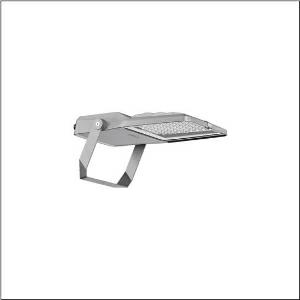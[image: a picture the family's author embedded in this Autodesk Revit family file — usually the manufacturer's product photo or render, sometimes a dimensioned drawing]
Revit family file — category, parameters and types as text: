
# Revit family: floodlight_fl_21_mini___pl43_5xa7776d2a1a_71d0
name_source: partatom
category: Lighting Fixtures
units: mm (PartAtom-declared; Revit-internal decimal feet)

## family parameters
Cut with Voids When Loaded = No
Host = Face
Light Source = No
Part Type = Normal
Room Calculation Point = No
Round Connector Dimension = Use Diameter
Shared = No

## types (1)
- --- (1 x LED, 18300 lm, 142.9 W, 3000K)
    Apparent Load = 143 VA
    CIE Flux Codes = 27 78 99 100 100
    Color Rendering = 70
    Color Temperature = 3000K
    Default Elevation = 1800 mm
    Description = Floodlight FL 21 mini, floodlight, primary light control with lens, of PMMA, primary optical cover: protective disc, of toughened safety glass, transparent, light distribution: PL43, light emission: direct distribution, installation type: surface-mounted, LED, High Power LED, rated luminous flux: 18.300lm, luminous efficacy: 128lm/W, light colour: 730, colour temperature: 3000K, control gear: Smart Interface (Zhaga), control: flexible luminous flux parameterisation, time-dependent luminous flux control, constant luminous flux control, overheat protection, pre-setting: logarithmic dimming characteristic, with terminal, 6-pole, mains connection: 220..240V, AC, 50/60Hz, start of lifetime: 143W, end of service life: 151W, reduction: 63W, luminaire housing, of diecast aluminium, powder-coated, Siteco® metallic grey (DB 702S), corrosivity category C5 mid according to DIN EN ISO 12944, suitable for swimming pools, chlorine-resistant, sealing non-destructively replaceable, mounting bracket, of steel, galvanised, powder-coated, Siteco® metallic grey (DB 702S), Smart Interface below and above, protection rating (complete): IP66, insulation class (complete): insulation class II (safety insulation), certification: CE, ENEC, VDE, protection symbol: D, impact resistance: IK08, permissible operating ambient temperature: -40..+40°C, permissible operating ambient temperature for outdoor applications: -40..+50°C, standard: DIN EN 12944, LABS conformity tested according to VDMA 24364:2018-05, packaging unit: 1 piece

Light Distribution: PL43
    Height = 70 mm
    Lamp = 1 x LED
    Lamp Light Flux = 18300 lm
    Lamp Power = 142.9 W
    Lamp count = 1
    Length = 485 mm
    Luminous efficacy = 128 lm/W
    Manufacturer = Siteco
    ModVariant = No
    Model = 5XA7776D2A1A
    Number of Poles = 1
    OnlyDefault = Yes
    Power Factor = 1
    Product Name = Floodlight FL 21 mini | PL43
    Product group = floodlight | pylon annexe
    ProductGroupID = 6200
    Protection Class = Protection class II
    Protection Degree = IP 66
    RLX_Detail_Level = 1
    RLX_Emergency_Light_Flux = 0 lm
    RLX_Emergency_Type = 0
    RLX_Emergency_Type_DB = No
    RlxData = <blob elided: 96189 chars, md5=3f9c6c30>
    Socket = socket
    Standby Power = 0 W
    System Light Flux = 18300 lm
    System Power = 143 W
    Type Comments = factory setting: luminous flux: 100 % | dim-lin: 254 | 730 mA
    Type Image = l_1006845.jpg
    URL = http://relux.com
    VarID = @adj_161024
    Voltage = 0 V
    Weight = 0.00 kg
    Width = 337 mm

## geometry (parser evidence)
native form markers: Blend x4, Sweep x13
no freeform markers — native parametric forms only
